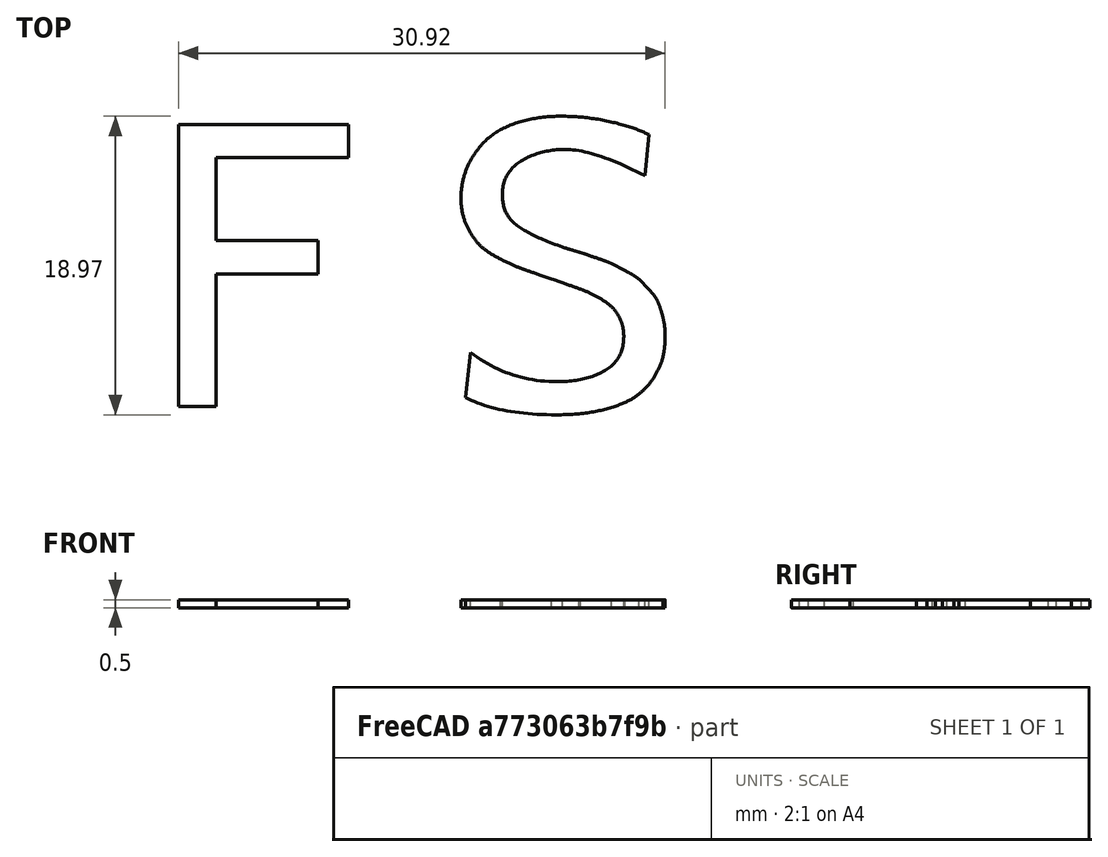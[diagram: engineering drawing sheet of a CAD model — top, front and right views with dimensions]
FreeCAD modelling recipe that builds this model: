
FCSTD DOCUMENT  (FreeCAD 0.18R16131 (Git))
Label: InterupteurPiscine
License: All rights reserved
LicenseURL: http://en.wikipedia.org/wiki/All_rights_reserved
objects: Part::Part2DObjectPython×2, Sketcher::SketchObject×1, PartDesign::Body×1, Part::Extrusion×1
note: 5 computed .brp shape members not serialized (recipe doc carries the construction recipe); baked Part::Feature solids carry a one-line shape summary decoded from their .brp

FEATURE [Part::Part2DObjectPython] ShapeString  # Draft 2D object (typed FeaturePython)
  FontFile = <path>
  Placement = pos=(2.22419,0.3,1.55792) rot=(0,0,1;0rad)
  Size = 10
  String = F S
  Tracking = 0
FEATURE [Part::Part2DObjectPython] Rectangle  # Draft 2D object (typed FeaturePython)
  ChamferSize = 0
  Columns = 1
  FilletRadius = 0
  Height = 36
  Length = 41
  MakeFace = true
  Placement = pos=(-16.9718,-16.8568,2.79382) rot=(-0.884822,-0.449124,-0.124009;0.345032rad)
  Rows = 1
FEATURE [Sketcher::SketchObject] Sketch
  MapMode = 5
  Support = -> [XY_Plane]
FEATURE [PartDesign::Body] Body
  Group = -> [Sketch]
  Origin = -> Origin
FEATURE [Part::Extrusion] Extrude
  Base = -> ShapeString
  Dir = (0,0,1)
  DirMode = 2
  FaceMakerClass = Part::FaceMakerBullseye
  LengthFwd = 0.5
  LengthRev = 0
  Solid = false
  Symmetric = false
note: 1 file-system path scrubbed to <path> (originals preserved in the JSON sidecar)
